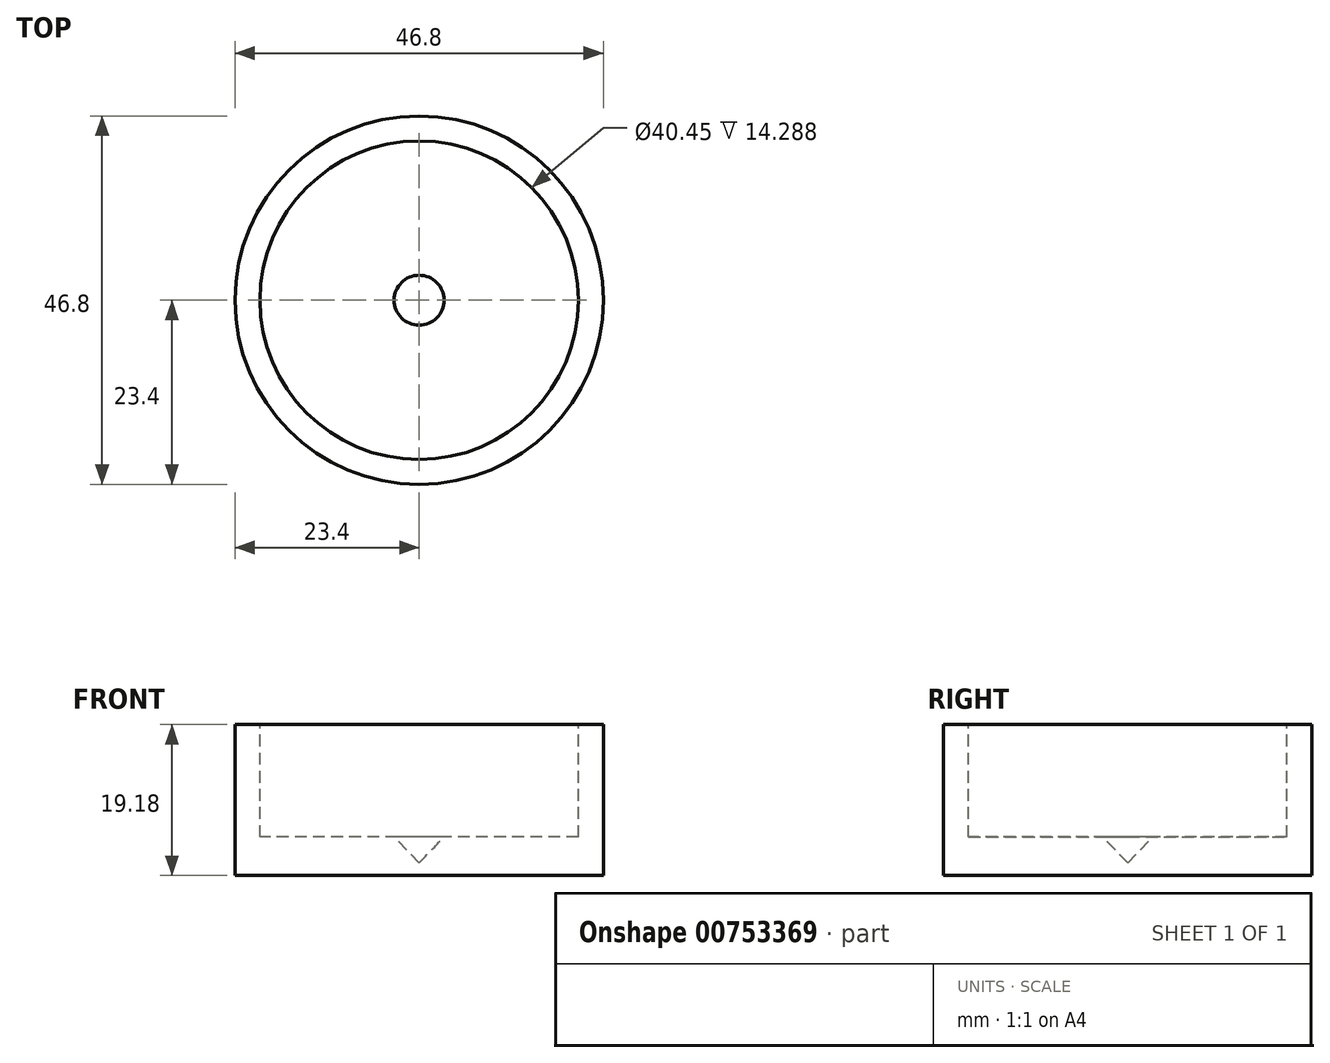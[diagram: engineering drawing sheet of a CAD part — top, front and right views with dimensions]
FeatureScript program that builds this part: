
annotation { "Feature Type Name" : "Feature", "Feature Type Description" : "" }
export const myFeature = defineFeature(function(context is Context, id is Id, definition is map)
    precondition{}
    {
        {
            var Q0;
            Q0=qCreatedBy(makeId("Front.planeOp"),FACE);
            var sketch = newSketch(context, id + "F0", { "sketchPlane" : qUnion([Q0])});
            skLineSegment(sketch, "E0", {"start": v(0, 30.07) * mm, "end": v(0, -26.5) * mm, "construction": true});
            skLineSegment(sketch, "E1", {"start": v(0, 0) * mm, "end": v(3.18, 3.3) * mm});
            skLineSegment(sketch, "E2", {"start": v(3.18, 3.3) * mm, "end": v(20.22, 3.3) * mm});
            skLineSegment(sketch, "E3", {"start": v(20.22, 3.3) * mm, "end": v(20.22, 17.59) * mm});
            skLineSegment(sketch, "E4", {"start": v(20.22, 17.59) * mm, "end": v(23.4, 17.59) * mm});
            skLineSegment(sketch, "E5", {"start": v(23.4, 17.59) * mm, "end": v(23.4, -1.59) * mm});
            skLineSegment(sketch, "E6", {"start": v(23.4, -1.59) * mm, "end": v(0, -1.59) * mm});
            skLineSegment(sketch, "E7", {"start": v(0, -1.59) * mm, "end": v(0, 0) * mm});
            skSolve(sketch);
        }
        {
            var Q0;
            Q0=makeQuery(id+"F0.imprint","IMPRINT",FACE,{"disambiguationData":[TD([[makeQuery(id+"F0.imprint","IMPRINT",EDGE,{"derivedFrom":sQuery(id+"F0.wireOp",EDGE,"E1")}),-1.0]])]});
            var Q1;
            Q1=sQuery(id+"F0.wireOp",EDGE,"E0");
            revolve(context, id + "F1", {"surfaceOperationType" : NewSurfaceOperationType.NEW, "entities" : qUnion([Q0]), "axis" : qUnion([Q1]), "revolveType" : RevolveType.FULL});
        }
        {
            var Q0;
            Q0=qCreatedBy(makeId("Front.planeOp"),FACE);
            cPlane(context, id + "F2", {"entities" : qUnion([Q0]), "cplaneType" : CPlaneType.OFFSET, "offset" : 25.4 * mm, "width" : 152.4 * mm, "height" : 152.4 * mm});
        }
    });
